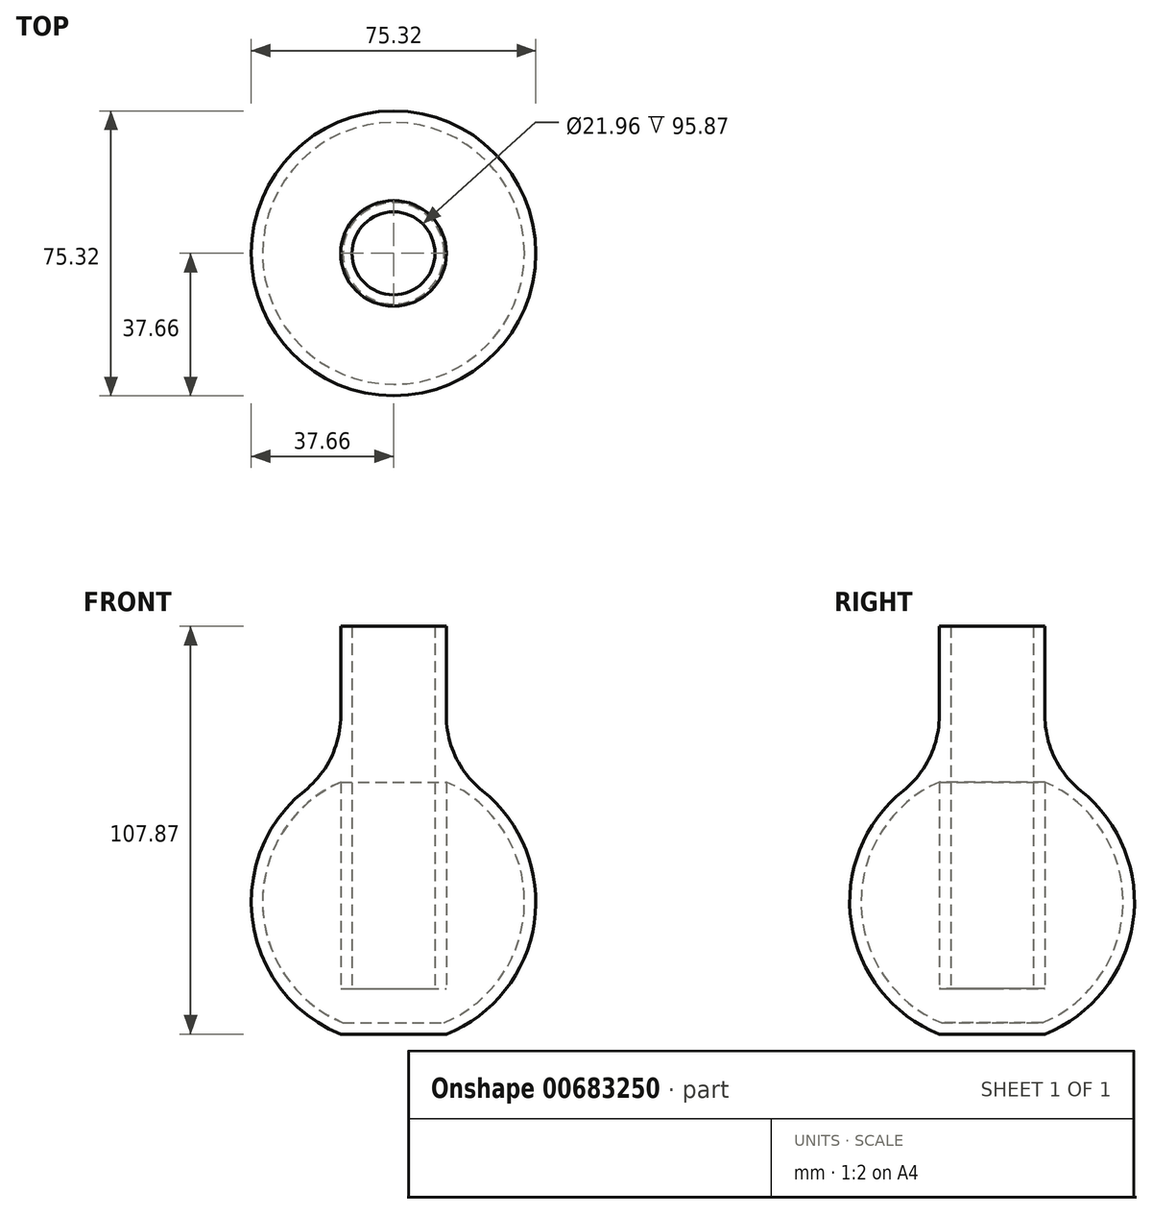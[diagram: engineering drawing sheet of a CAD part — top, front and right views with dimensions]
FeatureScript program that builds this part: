
annotation { "Feature Type Name" : "Feature", "Feature Type Description" : "" }
export const myFeature = defineFeature(function(context is Context, id is Id, definition is map)
    precondition{}
    {
        {
            var Q0;
            Q0=qCreatedBy(makeId("Right.planeOp"),FACE);
            var sketch = newSketch(context, id + "F0", { "sketchPlane" : qUnion([Q0])});
            skLineSegment(sketch, "E0", {"start": v(0, 0) * mm, "end": v(0, 3) * mm});
            skLineSegment(sketch, "E1", {"start": v(0, 0) * mm, "end": v(-13.98, 0) * mm});
            skPoint(sketch, "E2", {"position": v(-13.98, 0) * mm});
            skLineSegment(sketch, "E3", {"start": v(-13.98, 12) * mm, "end": v(-13.98, 66.69) * mm});
            skLineSegment(sketch, "E4", {"start": v(-13.98, 107.87) * mm, "end": v(-10.98, 107.87) * mm});
            skLineSegment(sketch, "E5", {"start": v(-13.98, 12) * mm, "end": v(-10.98, 12) * mm});
            skLineSegment(sketch, "E6", {"start": v(0, 3) * mm, "end": v(0, 0) * mm});
            skArc(sketch, "E7.trimOffspring", {"start": v(-13.98, 69.94) * mm, "mid": v(-37.66, 34.97) * mm, "end": v(-13.98, 0) * mm});
            skLineSegment(sketch, "E8.0", {"start": v(-10.98, 12) * mm, "end": v(-10.98, 107.87) * mm});
            skLineSegment(sketch, "E9.0", {"start": v(0, 3) * mm, "end": v(-13.39, 3) * mm});
            skArc(sketch, "E10.0", {"start": v(-13.98, 66.69) * mm, "mid": v(-34.66, 34.65) * mm, "end": v(-13.39, 3) * mm});
            skLineSegment(sketch, "E11.trimOffspring", {"start": v(-13.98, 69.94) * mm, "end": v(-13.98, 107.87) * mm});
            skLineSegment(sketch, "E12", {"start": v(-13.98, 0) * mm, "end": v(0, 0) * mm});
            skSolve(sketch);
        }
        {
            var Q0;
            Q0 = qSketchRegion(id + "F0", true);
            var Q1;
            Q1=sQuery(id+"F0.wireOp",EDGE,"E0");
            revolve(context, id + "F1", {"entities" : qUnion([Q0]), "axis" : qUnion([Q1]), "revolveType" : RevolveType.FULL});
        }
        {
            var Q0;
            Q0=makeQuery(id+"F1.opRevolve","SWEPT_EDGE",EDGE,{"disambiguationData":[OSD([sQuery(id+"F0.wireOp",EDGE,"E7.trimOffspring"),sQuery(id+"F0.wireOp",EDGE,"E11.trimOffspring")])]});
            fillet(context, id + "F2", {"entities" : qUnion([Q0]), "radius" : 25.4 * mm, "tangentPropagation" : true, "allowEdgeOverflow" : false});
        }
    });
